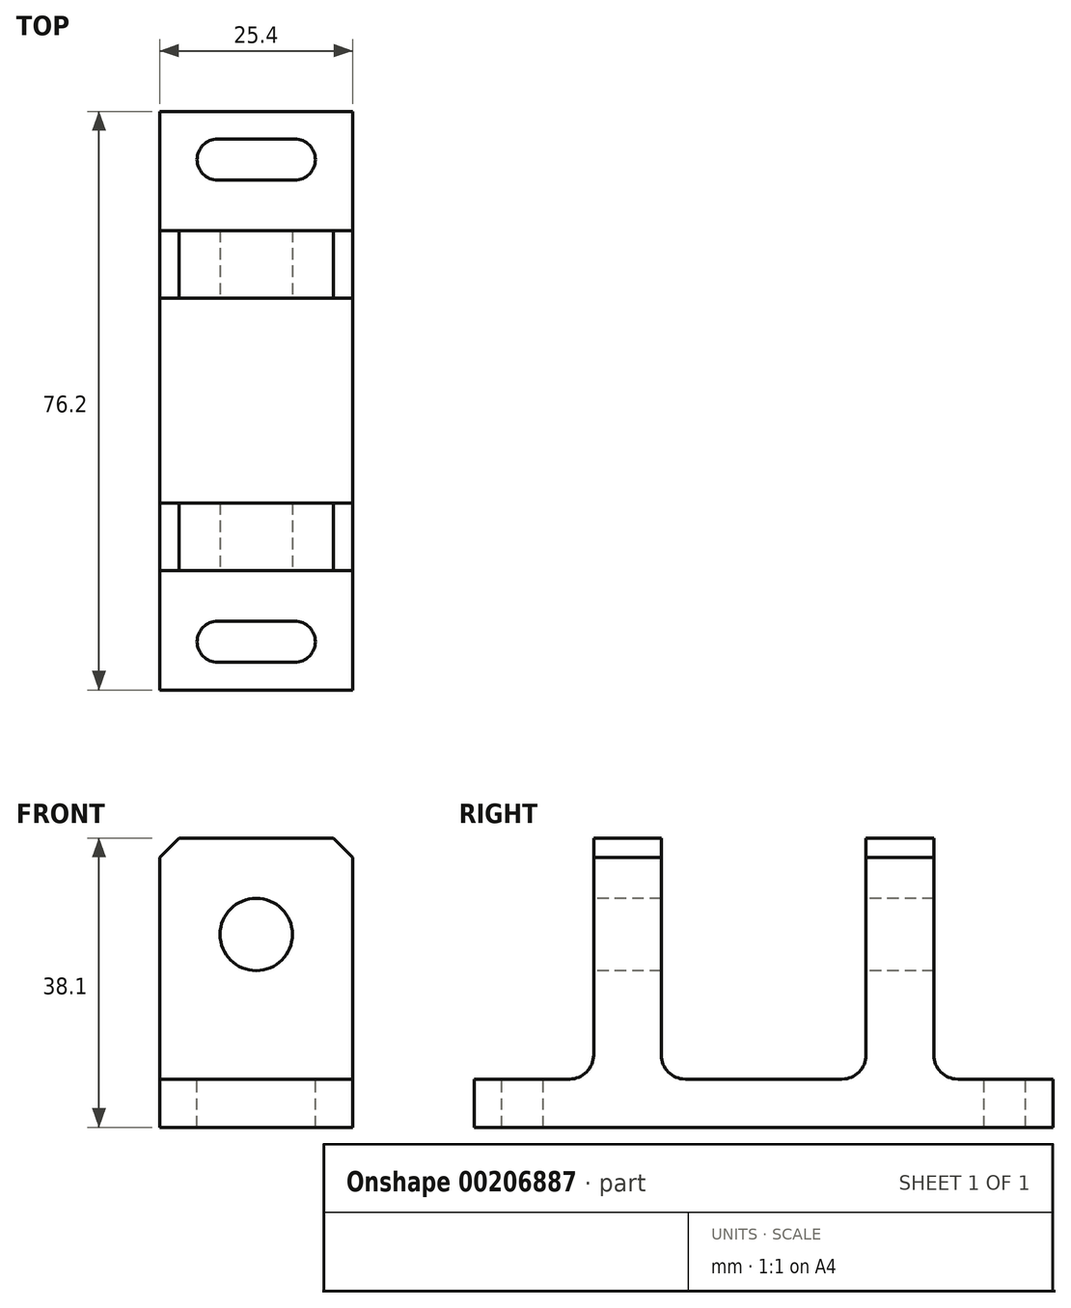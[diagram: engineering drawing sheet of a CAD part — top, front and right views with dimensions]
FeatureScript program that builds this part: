
annotation { "Feature Type Name" : "Feature", "Feature Type Description" : "" }
export const myFeature = defineFeature(function(context is Context, id is Id, definition is map)
    precondition{}
    {
        {
            var Q0;
            Q0=qCreatedBy(makeId("Right.planeOp"),FACE);
            var sketch = newSketch(context, id + "F0", { "sketchPlane" : qUnion([Q0])});
            skLineSegment(sketch, "E0", {"start": v(0, 0) * mm, "end": v(-38.1, 0) * mm});
            skLineSegment(sketch, "E1", {"start": v(-38.1, 0) * mm, "end": v(-38.1, 6.35) * mm});
            skLineSegment(sketch, "E2", {"start": v(-38.1, 6.35) * mm, "end": v(-25.56, 6.35) * mm});
            skLineSegment(sketch, "E3", {"start": v(-22.38, 9.52) * mm, "end": v(-22.38, 38.1) * mm});
            skLineSegment(sketch, "E4", {"start": v(-22.38, 38.1) * mm, "end": v(-13.5, 38.1) * mm});
            skLineSegment(sketch, "E5", {"start": v(-13.5, 38.1) * mm, "end": v(-13.5, 9.52) * mm});
            skLineSegment(sketch, "E6.MirrorCS", {"start": v(22.38, 38.1) * mm, "end": v(13.5, 38.1) * mm});
            skLineSegment(sketch, "E7.MirrorCS", {"start": v(22.38, 9.52) * mm, "end": v(22.38, 38.1) * mm});
            skLineSegment(sketch, "E8.MirrorCS", {"start": v(38.1, 6.35) * mm, "end": v(25.56, 6.35) * mm});
            skLineSegment(sketch, "E9.MirrorCS", {"start": v(38.1, 0) * mm, "end": v(38.1, 6.35) * mm});
            skLineSegment(sketch, "E10.MirrorCS", {"start": v(0, 0) * mm, "end": v(38.1, 0) * mm});
            skLineSegment(sketch, "E11", {"start": v(-10.32, 6.35) * mm, "end": v(0, 6.35) * mm});
            skLineSegment(sketch, "E12.MirrorCS", {"start": v(10.32, 6.35) * mm, "end": v(0, 6.35) * mm});
            skLineSegment(sketch, "E13.MirrorCS", {"start": v(13.5, 38.1) * mm, "end": v(13.5, 9.53) * mm});
            skPoint(sketch, "E14.visualSharp", {"position": v(-22.38, 6.35) * mm});
            skArc(sketch, "E14.filletArc", {"start": v(-25.56, 6.35) * mm, "mid": v(-23.31, 7.28) * mm, "end": v(-22.38, 9.52) * mm});
            skPoint(sketch, "E15.visualSharp", {"position": v(-13.5, 6.35) * mm});
            skArc(sketch, "E15.filletArc", {"start": v(-13.5, 9.52) * mm, "mid": v(-12.56, 7.28) * mm, "end": v(-10.32, 6.35) * mm});
            skPoint(sketch, "E16.visualSharp", {"position": v(13.5, 6.35) * mm});
            skArc(sketch, "E16.filletArc", {"start": v(10.32, 6.35) * mm, "mid": v(12.56, 7.28) * mm, "end": v(13.5, 9.53) * mm});
            skPoint(sketch, "E17.visualSharp", {"position": v(22.38, 6.35) * mm});
            skArc(sketch, "E17.filletArc", {"start": v(22.38, 9.52) * mm, "mid": v(23.31, 7.28) * mm, "end": v(25.56, 6.35) * mm});
            skSolve(sketch);
        }
        {
            var Q0;
            Q0=qSketchRegion(id+"F0",true);
            extrude(context, id + "F1", {"entities" : qUnion([Q0]), "endBound" : BoundingType.SYMMETRIC, "depth" : 25.4 * mm});
        }
        {
            var Q0;
            Q0=makeQuery(id+"F1.opExtrude","SWEPT_FACE",FACE,{"disambiguationData":[OSD([sQuery(id+"F0.wireOp",EDGE,"E3")])]});
            var sketch = newSketch(context, id + "F2", { "sketchPlane" : qUnion([Q0])});
            skCircle(sketch, "E18", {"center": v(0, 25.4) * mm, "radius": 4.76 * mm});
            skSolve(sketch);
        }
        {
            var Q0;
            Q0=qSketchRegion(id+"F2",true);
            var Q1;
            Q1=makeQuery(id+"F1.opExtrude","SWEPT_FACE",FACE,{"disambiguationData":[OSD([sQuery(id+"F0.wireOp",EDGE,"E7.MirrorCS")])]});
            extrude(context, id + "F3", {"entities" : qUnion([Q0]), "operationType" : NewBodyOperationType.REMOVE, "endBound" : BoundingType.UP_TO_SURFACE, "oppositeDirection" : true, "endBoundEntityFace" : qUnion([Q1]), "depth" : 25.4 * mm});
        }
        {
            var Q0;
            Q0=makeQuery(id+"F1.opExtrude","SWEPT_FACE",FACE,{"disambiguationData":[OSD([sQuery(id+"F0.wireOp",EDGE,"E8.MirrorCS")])]});
            var sketch = newSketch(context, id + "F4", { "sketchPlane" : qUnion([Q0])});
            skLineSegment(sketch, "E19", {"start": v(-5.08, 31.75) * mm, "end": v(5.08, 31.75) * mm});
            skArc(sketch, "E20.0.startCap", {"start": v(-5.08, 29.05) * mm, "mid": v(-7.78, 31.75) * mm, "end": v(-5.08, 34.45) * mm});
            skArc(sketch, "E20.0.endCap", {"start": v(5.08, 34.45) * mm, "mid": v(7.78, 31.75) * mm, "end": v(5.08, 29.05) * mm});
            skLineSegment(sketch, "E20.0.left", {"start": v(-5.08, 34.45) * mm, "end": v(5.08, 34.45) * mm});
            skLineSegment(sketch, "E20.0.right", {"start": v(-5.08, 29.05) * mm, "end": v(5.08, 29.05) * mm});
            skLineSegment(sketch, "E21.MirrorCS", {"start": v(-5.08, -34.45) * mm, "end": v(5.08, -34.45) * mm});
            skArc(sketch, "E22.MirrorCS", {"start": v(-5.08, -29.05) * mm, "mid": v(-7.78, -31.75) * mm, "end": v(-5.08, -34.45) * mm});
            skLineSegment(sketch, "E23.MirrorCS", {"start": v(-5.08, -29.05) * mm, "end": v(5.08, -29.05) * mm});
            skArc(sketch, "E24.MirrorCS", {"start": v(5.08, -34.45) * mm, "mid": v(7.78, -31.75) * mm, "end": v(5.08, -29.05) * mm});
            skPoint(sketch, "E25", {"position": v(0, 31.75) * mm});
            skPoint(sketch, "E26", {"position": v(0, -31.75) * mm});
            skLineSegment(sketch, "E27", {"start": v(0, -29.05) * mm, "end": v(0, -34.45) * mm});
            skSolve(sketch);
        }
        {
            var Q0;
            Q0=qSketchRegion(id+"F4",true);
            extrude(context, id + "F5", {"entities" : qUnion([Q0]), "operationType" : NewBodyOperationType.REMOVE, "endBound" : BoundingType.UP_TO_NEXT, "oppositeDirection" : true, "depth" : 25.4 * mm});
        }
        {
            var Q0;
            Q0=makeQuery(id+"F1.opExtrude","CAP_EDGE",EDGE,{"disambiguationData":[OSD([sQuery(id+"F0.wireOp",EDGE,"E4")])],"isStart":false});
            var Q1;
            Q1=makeQuery(id+"F1.opExtrude","CAP_EDGE",EDGE,{"disambiguationData":[OSD([sQuery(id+"F0.wireOp",EDGE,"E6.MirrorCS")])],"isStart":false});
            var Q2;
            Q2=makeQuery(id+"F1.opExtrude","CAP_EDGE",EDGE,{"disambiguationData":[OSD([sQuery(id+"F0.wireOp",EDGE,"E4")])],"isStart":true});
            var Q3;
            Q3=makeQuery(id+"F1.opExtrude","CAP_EDGE",EDGE,{"disambiguationData":[OSD([sQuery(id+"F0.wireOp",EDGE,"E6.MirrorCS")])],"isStart":true});
            chamfer(context, id + "F6", {"entities" : qUnion([Q0, Q1, Q2, Q3]), "width" : 2.54 * mm, "tangentPropagation" : true});
        }
    });
